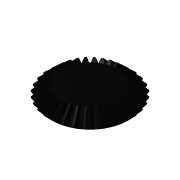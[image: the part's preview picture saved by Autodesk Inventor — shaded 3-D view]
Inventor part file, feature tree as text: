
AUTODESK INVENTOR PART (.ipt)
format: ipt  version: 2016 (Build 200138000, 138)  size: 549,888 bytes
history: native  units: mm
features: other x16, sketch x1
ambient origin geometry x6: Origin, XZ Plane, X Axis, Y Axis, Z Axis, Center Point
bodies: Solid1 (feature_tree)
feature tree (17):
  other  "Top Point"
  other  "Mesh Plane2"
  other  "Teeth Body"
  other  "Start Point"
  other  "Tooth Plane"
  other  "Start Sketch"
  other  "End Point"
  other  "Fix Body"
  other  "Mesh Plane"
  other  "Top Plane"
  other  "Teeth Body Sketch"
  other  "End Plane"
  other  "End Sketch"
  other  "Body Sketch"
  sketch  "Sketch6"  dims[d0=47.811765mm d1=45.276163mm d2=49.924766mm d3=9.525mm d4=22.849382mm d5=90.0deg d7=12.077204mm d8=12.386496mm d9=29.30193mm d11=9.689353mm d12=8.627964mm d15=8.848923mm d16=20.933322mm d17=0.0mm d18=90.0deg d19=0.0mm d20=90.0deg d21=320.0mm d22=360.0deg d46=90.0deg d47=90.0deg d48=0.0mm d49=0.0mm d50=90.0deg d51=0.981748mm d52=0.0mm d53=0.0mm d54=0.0mm d57=36.288258mm d58=31.620635mm d59=25.92436mm d60=22.589806mm d88=0.0mm d89=0.0mm]
  other  "Srf1"
  other  "Pitch Diameter"
